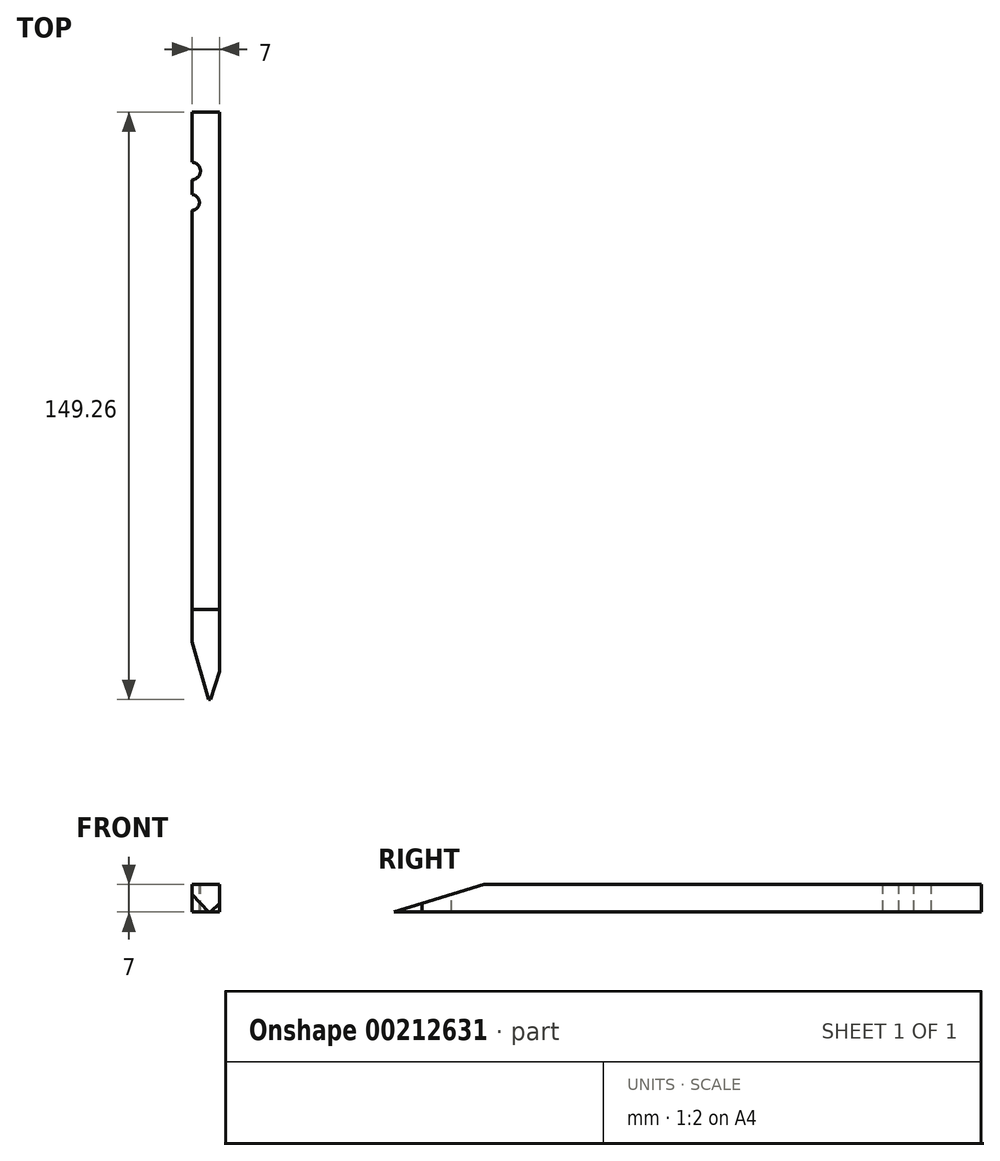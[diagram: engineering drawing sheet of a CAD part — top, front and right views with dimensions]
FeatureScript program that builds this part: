
annotation { "Feature Type Name" : "Feature", "Feature Type Description" : "" }
export const myFeature = defineFeature(function(context is Context, id is Id, definition is map)
    precondition{}
    {
        {
            var Q0;
            Q0=qCreatedBy(makeId("Top.planeOp"),FACE);
            var sketch = newSketch(context, id + "F0", { "sketchPlane" : qUnion([Q0])});
            skLineSegment(sketch, "E0.bottom", {"start": v(-3.5, 75) * mm, "end": v(3.5, 75) * mm});
            skLineSegment(sketch, "E0.top", {"start": v(-3.5, -75) * mm, "end": v(3.5, -75) * mm});
            skLineSegment(sketch, "E0.left", {"start": v(-3.5, 75) * mm, "end": v(-3.5, -75) * mm});
            skLineSegment(sketch, "E0.right", {"start": v(3.5, 75) * mm, "end": v(3.5, -75) * mm});
            skSolve(sketch);
        }
        {
            var Q0;
            Q0=qCreatedBy(makeId("Top.planeOp"),FACE);
            var sketch = newSketch(context, id + "F1", { "sketchPlane" : qUnion([Q0])});
            skLineSegment(sketch, "E1", {"start": v(-7.53, -46) * mm, "end": v(5.15, -89.07) * mm});
            skLineSegment(sketch, "E2", {"start": v(5.15, -89.07) * mm, "end": v(-12.07, -91.44) * mm});
            skLineSegment(sketch, "E3", {"start": v(-12.07, -91.44) * mm, "end": v(-7.53, -46) * mm});
            skSolve(sketch);
        }
        {
            var Q0;
            Q0=qCreatedBy(makeId("Top.planeOp"),FACE);
            var sketch = newSketch(context, id + "F2", { "sketchPlane" : qUnion([Q0])});
            skLineSegment(sketch, "E4", {"start": v(5.72, -60.01) * mm, "end": v(-0.81, -80.84) * mm});
            skLineSegment(sketch, "E5", {"start": v(5.72, -60.01) * mm, "end": v(10.17, -82.73) * mm});
            skLineSegment(sketch, "E6", {"start": v(10.17, -82.73) * mm, "end": v(-0.81, -80.84) * mm});
            skSolve(sketch);
        }
        {
            var Q0;
            Q0=qCreatedBy(makeId("Right.planeOp"),FACE);
            var sketch = newSketch(context, id + "F3", { "sketchPlane" : qUnion([Q0])});
            skLineSegment(sketch, "E7", {"start": v(-84.12, -3.02) * mm, "end": v(-44.65, 9.08) * mm});
            skLineSegment(sketch, "E8", {"start": v(-44.65, 9.08) * mm, "end": v(-83.84, 23.08) * mm});
            skLineSegment(sketch, "E9", {"start": v(-83.84, 23.08) * mm, "end": v(-84.12, -3.02) * mm});
            skSolve(sketch);
        }
        {
            var Q0;
            Q0=qCreatedBy(makeId("Top.planeOp"),FACE);
            var sketch = newSketch(context, id + "F4", { "sketchPlane" : qUnion([Q0])});
            skCircle(sketch, "E10", {"center": v(-3.59, 60) * mm, "radius": 2.25 * mm});
            skCircle(sketch, "E11", {"center": v(-3.59, 52) * mm, "radius": 2 * mm});
            skSolve(sketch);
        }
        {
            var Q0;
            Q0 = qSketchRegion(id + "F0", true);
            extrude(context, id + "F5", {"entities" : qUnion([Q0]), "depth" : 7 * mm});
        }
        {
            var Q0;
            Q0 = qSketchRegion(id + "F1", true);
            var Q1;
            Q1 = qSketchRegion(id + "F2", true);
            extrude(context, id + "F6", {"entities" : qUnion([Q0, Q1]), "operationType" : NewBodyOperationType.REMOVE, "depth" : 25 * mm, "hasSecondDirection" : true, "secondDirectionOppositeDirection" : true, "secondDirectionDepth" : 25 * mm});
        }
        {
            var Q0;
            Q0 = qSketchRegion(id + "F3", true);
            extrude(context, id + "F7", {"entities" : qUnion([Q0]), "operationType" : NewBodyOperationType.REMOVE, "oppositeDirection" : true, "depth" : 25 * mm, "hasSecondDirection" : true, "secondDirectionOppositeDirection" : false, "secondDirectionDepth" : 25 * mm});
        }
        {
            var Q0;
            Q0 = qSketchRegion(id + "F4", true);
            extrude(context, id + "F8", {"entities" : qUnion([Q0]), "operationType" : NewBodyOperationType.REMOVE, "oppositeDirection" : true, "depth" : 25 * mm, "hasSecondDirection" : true, "secondDirectionOppositeDirection" : false, "secondDirectionDepth" : 25 * mm});
        }
    });
